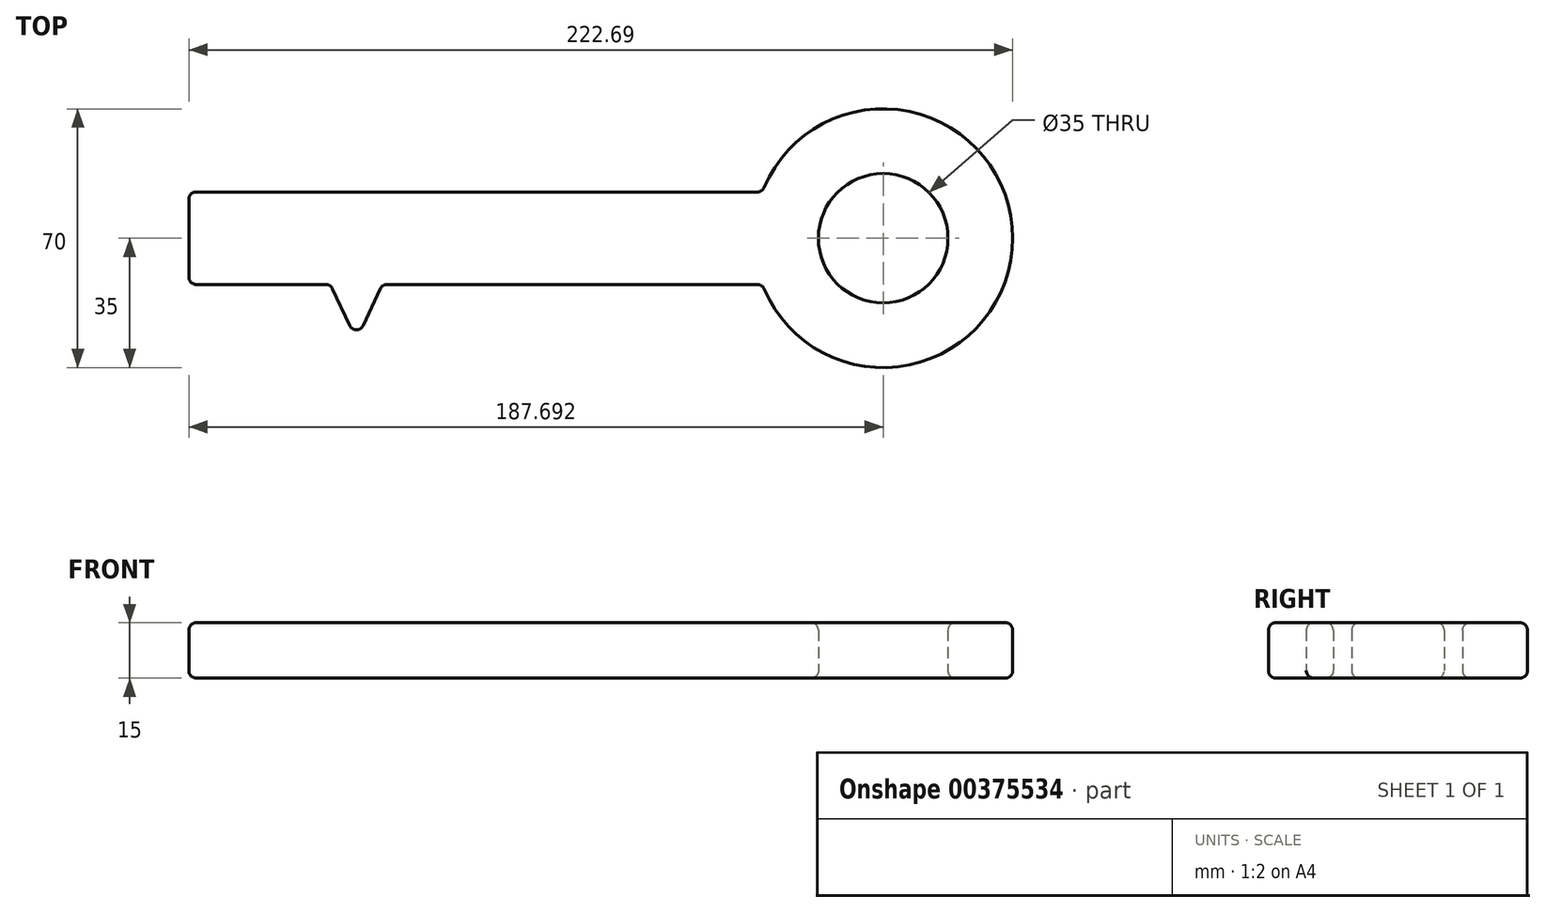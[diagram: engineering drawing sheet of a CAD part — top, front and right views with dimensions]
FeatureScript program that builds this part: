
annotation { "Feature Type Name" : "Feature", "Feature Type Description" : "" }
export const myFeature = defineFeature(function(context is Context, id is Id, definition is map)
    precondition{}
    {
        {
            var Q0;
            Q0=qCreatedBy(makeId("Top.planeOp"),FACE);
            var sketch = newSketch(context, id + "F0", { "sketchPlane" : qUnion([Q0])});
            skLineSegment(sketch, "E0.bottom", {"start": v(-94.78, 40) * mm, "end": v(60.22, 40) * mm});
            skLineSegment(sketch, "E0.top", {"start": v(-94.78, 15) * mm, "end": v(60.22, 15) * mm});
            skLineSegment(sketch, "E0.left", {"start": v(-94.78, 40) * mm, "end": v(-94.78, 15) * mm});
            skLineSegment(sketch, "E1.bottom", {"start": v(-94.49, 15) * mm, "end": v(-84.49, 15) * mm});
            skLineSegment(sketch, "E1.top", {"start": v(-94.49, -15) * mm, "end": v(-84.49, -15) * mm});
            skLineSegment(sketch, "E1.left", {"start": v(-94.49, 15) * mm, "end": v(-94.49, -15) * mm});
            skLineSegment(sketch, "E1.right", {"start": v(-84.49, 15) * mm, "end": v(-84.49, -15) * mm});
            skLineSegment(sketch, "E2.bottom", {"start": v(-74.49, 15) * mm, "end": v(-66.49, 15) * mm});
            skLineSegment(sketch, "E2.top", {"start": v(-74.49, 0) * mm, "end": v(-66.49, 0) * mm});
            skLineSegment(sketch, "E2.left", {"start": v(-74.49, 15) * mm, "end": v(-74.49, 0) * mm});
            skLineSegment(sketch, "E2.right", {"start": v(-66.49, 15) * mm, "end": v(-66.49, 0) * mm});
            skLineSegment(sketch, "E3", {"start": v(-56.49, 15) * mm, "end": v(-49.49, 0) * mm});
            skLineSegment(sketch, "E4", {"start": v(-49.49, 0) * mm, "end": v(-42.49, 15) * mm});
            skArc(sketch, "E5", {"start": v(60.22, 15) * mm, "mid": v(127.91, 27.5) * mm, "end": v(60.22, 40) * mm});
            skCircle(sketch, "E6", {"center": v(92.91, 27.5) * mm, "radius": 17.5 * mm});
            skLineSegment(sketch, "E7", {"start": v(-94.78, 27.5) * mm, "end": v(92.91, 27.5) * mm, "construction": true});
            skSolve(sketch);
        }
        {
            var Q0;
            Q0=makeQuery(id+"F0.imprint","IMPRINT",FACE,{"disambiguationData":[TD([[makeQuery(id+"F0.imprint","IMPRINT",EDGE,{"derivedFrom":sQuery(id+"F0.wireOp",EDGE,"E0.bottom")}),-1.0]])]});
            var Q1;
            Q1=makeQuery(id+"F0.imprint","IMPRINT",FACE,{"disambiguationData":[TD([[makeQuery(id+"F0.imprint","IMPRINT",EDGE,{"derivedFrom":sQuery(id+"F0.wireOp",EDGE,"E1.bottom")}),-1.0]])]});
            var Q2;
            Q2=makeQuery(id+"F0.imprint","IMPRINT",FACE,{"disambiguationData":[TD([[makeQuery(id+"F0.imprint","IMPRINT",EDGE,{"derivedFrom":sQuery(id+"F0.wireOp",EDGE,"E2.bottom")}),-1.0]])]});
            var Q3;
            {var subQ0=sQuery(id+"F0.wireOp",EDGE,"E3");Q3=makeQuery(id+"F0.imprint","IMPRINT",FACE,{"disambiguationData":[TD([[makeQuery(id+"F0.imprint","IMPRINT",EDGE,{"derivedFrom":subQ0}),1.0]])]});}
            extrude(context, id + "F1", {"entities" : qUnion([Q0, Q1, Q2, Q3]), "depth" : 15 * mm});
        }
        {
            var Q0;
            Q0=makeQuery(id+"F1.opExtrude","CAP_EDGE",EDGE,{"disambiguationData":[OSD([sQuery(id+"F0.wireOp",EDGE,"E0.bottom")])],"isStart":false});
            var Q1;
            Q1=makeQuery(id+"F1.opExtrude","CAP_EDGE",EDGE,{"disambiguationData":[OSD([sQuery(id+"F0.wireOp",EDGE,"E1.top")])],"isStart":false});
            var Q2;
            Q2=makeQuery(id+"F1.opExtrude","CAP_EDGE",EDGE,{"disambiguationData":[OSD([sQuery(id+"F0.wireOp",EDGE,"E1.right")])],"isStart":false});
            var Q3;
            {var subQ0=sQuery(id+"F0.wireOp",EDGE,"E0.top");Q3=makeQuery(id+"F1.opExtrude","CAP_EDGE",EDGE,{"disambiguationData":[OSD([subQ0]),TDD([makeQuery(id+"F0.imprint","IMPRINT",EDGE,{"disambiguationData":[TD([[makeQuery(id+"F0.imprint","INTERSECT",VERTEX,{"derivedFrom":[subQ0,sQuery(id+"F0.wireOp",EDGE,"E1.bottom"),sQuery(id+"F0.wireOp",EDGE,"E1.right")]}),-1.0]])],"derivedFrom":subQ0})])],"isStart":false});}
            var Q4;
            {var subQ0=sQuery(id+"F0.wireOp",EDGE,"E0.top");Q4=makeQuery(id+"F1.opExtrude","CAP_EDGE",EDGE,{"disambiguationData":[OSD([subQ0]),TDD([makeQuery(id+"F0.imprint","IMPRINT",EDGE,{"disambiguationData":[TD([[makeQuery(id+"F0.imprint","INTERSECT",VERTEX,{"derivedFrom":[subQ0,sQuery(id+"F0.wireOp",EDGE,"E3")]}),1.0]])],"derivedFrom":subQ0})])],"isStart":false});}
            var Q5;
            Q5=makeQuery(id+"F1.opExtrude","CAP_EDGE",EDGE,{"disambiguationData":[OSD([sQuery(id+"F0.wireOp",EDGE,"E4")])],"isStart":false});
            var Q6;
            Q6=makeQuery(id+"F1.opExtrude","CAP_EDGE",EDGE,{"disambiguationData":[OSD([sQuery(id+"F0.wireOp",EDGE,"E5")])],"isStart":false});
            var Q7;
            Q7=makeQuery(id+"F1.opExtrude","CAP_EDGE",EDGE,{"disambiguationData":[OSD([sQuery(id+"F0.wireOp",EDGE,"E2.top")])],"isStart":false});
            var Q8;
            Q8=makeQuery(id+"F1.opExtrude","CAP_EDGE",EDGE,{"disambiguationData":[OSD([sQuery(id+"F0.wireOp",EDGE,"E1.left")])],"isStart":false});
            var Q9;
            Q9=makeQuery(id+"F1.opExtrude","CAP_EDGE",EDGE,{"disambiguationData":[OSD([sQuery(id+"F0.wireOp",EDGE,"E2.left")])],"isStart":false});
            var Q10;
            Q10=makeQuery(id+"F1.opExtrude","CAP_EDGE",EDGE,{"disambiguationData":[OSD([sQuery(id+"F0.wireOp",EDGE,"E2.right")])],"isStart":false});
            var Q11;
            Q11=makeQuery(id+"F1.opExtrude","CAP_EDGE",EDGE,{"disambiguationData":[OSD([sQuery(id+"F0.wireOp",EDGE,"E5")])],"isStart":true});
            var Q12;
            Q12=makeQuery(id+"F1.opExtrude","CAP_EDGE",EDGE,{"disambiguationData":[OSD([sQuery(id+"F0.wireOp",EDGE,"E6")])],"isStart":true});
            var Q13;
            Q13=makeQuery(id+"F1.opExtrude","SWEPT_FACE",FACE,{"disambiguationData":[OSD([sQuery(id+"F0.wireOp",EDGE,"E6")])]});
            var Q14;
            {var subQ0=sQuery(id+"F0.wireOp",EDGE,"E0.top");Q14=makeQuery(id+"F1.opExtrude","CAP_EDGE",EDGE,{"disambiguationData":[OSD([subQ0]),TDD([makeQuery(id+"F0.imprint","IMPRINT",EDGE,{"disambiguationData":[TD([[makeQuery(id+"F0.imprint","INTERSECT",VERTEX,{"derivedFrom":[subQ0,sQuery(id+"F0.wireOp",EDGE,"E5")]}),1.0]])],"derivedFrom":subQ0})])],"isStart":true});}
            var Q15;
            {var subQ0=sQuery(id+"F0.wireOp",EDGE,"E0.top");Q15=makeQuery(id+"F1.opExtrude","CAP_EDGE",EDGE,{"disambiguationData":[OSD([subQ0]),TDD([makeQuery(id+"F0.imprint","IMPRINT",EDGE,{"disambiguationData":[TD([[makeQuery(id+"F0.imprint","INTERSECT",VERTEX,{"derivedFrom":[subQ0,sQuery(id+"F0.wireOp",EDGE,"E5")]}),1.0]])],"derivedFrom":subQ0})])],"isStart":false});}
            var Q16;
            Q16=makeQuery(id+"F1.opExtrude","SWEPT_EDGE",EDGE,{"disambiguationData":[OSD([sQuery(id+"F0.wireOp",EDGE,"E0.bottom"),sQuery(id+"F0.wireOp",EDGE,"E5")])]});
            var Q17;
            Q17=makeQuery(id+"F1.opExtrude","CAP_EDGE",EDGE,{"disambiguationData":[OSD([sQuery(id+"F0.wireOp",EDGE,"E4")])],"isStart":true});
            var Q18;
            Q18=makeQuery(id+"F1.opExtrude","SWEPT_EDGE",EDGE,{"disambiguationData":[OSD([sQuery(id+"F0.wireOp",EDGE,"E0.top"),sQuery(id+"F0.wireOp",EDGE,"E4")])]});
            var Q19;
            Q19=makeQuery(id+"F1.opExtrude","SWEPT_EDGE",EDGE,{"disambiguationData":[OSD([sQuery(id+"F0.wireOp",EDGE,"E0.top"),sQuery(id+"F0.wireOp",EDGE,"E3")])]});
            var Q20;
            Q20=makeQuery(id+"F1.opExtrude","CAP_EDGE",EDGE,{"disambiguationData":[OSD([sQuery(id+"F0.wireOp",EDGE,"E3")])],"isStart":true});
            var Q21;
            Q21=makeQuery(id+"F1.opExtrude","CAP_EDGE",EDGE,{"disambiguationData":[OSD([sQuery(id+"F0.wireOp",EDGE,"E0.bottom")])],"isStart":true});
            var Q22;
            Q22=makeQuery(id+"F1.opExtrude","CAP_EDGE",EDGE,{"disambiguationData":[OSD([sQuery(id+"F0.wireOp",EDGE,"E6")])],"isStart":false});
            var Q23;
            Q23=makeQuery(id+"F1.opExtrude","SWEPT_EDGE",EDGE,{"disambiguationData":[OSD([sQuery(id+"F0.wireOp",EDGE,"E0.bottom"),sQuery(id+"F0.wireOp",EDGE,"E0.left")])]});
            var Q24;
            Q24=makeQuery(id+"F1.opExtrude","CAP_EDGE",EDGE,{"disambiguationData":[OSD([sQuery(id+"F0.wireOp",EDGE,"E0.left")])],"isStart":true});
            var Q25;
            Q25=makeQuery(id+"F1.opExtrude","CAP_EDGE",EDGE,{"disambiguationData":[OSD([sQuery(id+"F0.wireOp",EDGE,"E2.right")])],"isStart":true});
            var Q26;
            {var subQ0=sQuery(id+"F0.wireOp",EDGE,"E0.top");Q26=makeQuery(id+"F1.opExtrude","CAP_EDGE",EDGE,{"disambiguationData":[OSD([subQ0]),TDD([makeQuery(id+"F0.imprint","IMPRINT",EDGE,{"disambiguationData":[TD([[makeQuery(id+"F0.imprint","INTERSECT",VERTEX,{"derivedFrom":[subQ0,sQuery(id+"F0.wireOp",EDGE,"E1.bottom"),sQuery(id+"F0.wireOp",EDGE,"E1.right")]}),-1.0]])],"derivedFrom":subQ0})])],"isStart":true});}
            var Q27;
            Q27=makeQuery(id+"F1.opExtrude","CAP_EDGE",EDGE,{"disambiguationData":[OSD([sQuery(id+"F0.wireOp",EDGE,"E1.right")])],"isStart":true});
            var Q28;
            Q28=makeQuery(id+"F1.opExtrude","SWEPT_EDGE",EDGE,{"disambiguationData":[OSD([sQuery(id+"F0.wireOp",EDGE,"E3"),sQuery(id+"F0.wireOp",EDGE,"E4")])]});
            var Q29;
            Q29=makeQuery(id+"F1.opExtrude","SWEPT_EDGE",EDGE,{"disambiguationData":[OSD([sQuery(id+"F0.wireOp",EDGE,"E2.top"),sQuery(id+"F0.wireOp",EDGE,"E2.left")])]});
            var Q30;
            Q30=makeQuery(id+"F1.opExtrude","CAP_EDGE",EDGE,{"disambiguationData":[OSD([sQuery(id+"F0.wireOp",EDGE,"E1.left")])],"isStart":true});
            var Q31;
            Q31=makeQuery(id+"F1.opExtrude","SWEPT_EDGE",EDGE,{"disambiguationData":[OSD([sQuery(id+"F0.wireOp",EDGE,"E1.top"),sQuery(id+"F0.wireOp",EDGE,"E1.right")])]});
            var Q32;
            Q32=makeQuery(id+"F1.opExtrude","SWEPT_EDGE",EDGE,{"disambiguationData":[OSD([sQuery(id+"F0.wireOp",EDGE,"E1.top"),sQuery(id+"F0.wireOp",EDGE,"E1.left")])]});
            var Q33;
            Q33=makeQuery(id+"F1.opExtrude","CAP_EDGE",EDGE,{"disambiguationData":[OSD([sQuery(id+"F0.wireOp",EDGE,"E3")])],"isStart":false});
            var Q34;
            Q34=makeQuery(id+"F1.opExtrude","SWEPT_EDGE",EDGE,{"disambiguationData":[OSD([sQuery(id+"F0.wireOp",EDGE,"E0.top"),sQuery(id+"F0.wireOp",EDGE,"E0.left")])]});
            var Q35;
            Q35=makeQuery(id+"F1.opExtrude","SWEPT_EDGE",EDGE,{"disambiguationData":[OSD([sQuery(id+"F0.wireOp",EDGE,"E0.top"),sQuery(id+"F0.wireOp",EDGE,"E2.bottom"),sQuery(id+"F0.wireOp",EDGE,"E2.right")])]});
            var Q36;
            Q36=makeQuery(id+"F1.opExtrude","SWEPT_EDGE",EDGE,{"disambiguationData":[OSD([sQuery(id+"F0.wireOp",EDGE,"E2.top"),sQuery(id+"F0.wireOp",EDGE,"E2.right")])]});
            var Q37;
            Q37=makeQuery(id+"F1.opExtrude","SWEPT_EDGE",EDGE,{"disambiguationData":[OSD([sQuery(id+"F0.wireOp",EDGE,"E0.top"),sQuery(id+"F0.wireOp",EDGE,"E1.bottom"),sQuery(id+"F0.wireOp",EDGE,"E1.right")])]});
            var Q38;
            Q38=makeQuery(id+"F1.opExtrude","SWEPT_EDGE",EDGE,{"disambiguationData":[OSD([sQuery(id+"F0.wireOp",EDGE,"E0.top"),sQuery(id+"F0.wireOp",EDGE,"E5")])]});
            var Q39;
            Q39=makeQuery(id+"F1.opExtrude","CAP_EDGE",EDGE,{"disambiguationData":[OSD([sQuery(id+"F0.wireOp",EDGE,"E2.left")])],"isStart":true});
            var Q40;
            {var subQ0=sQuery(id+"F0.wireOp",EDGE,"E0.top");Q40=makeQuery(id+"F1.opExtrude","CAP_EDGE",EDGE,{"disambiguationData":[OSD([subQ0]),TDD([makeQuery(id+"F0.imprint","IMPRINT",EDGE,{"disambiguationData":[TD([[makeQuery(id+"F0.imprint","INTERSECT",VERTEX,{"derivedFrom":[subQ0,sQuery(id+"F0.wireOp",EDGE,"E3")]}),1.0]])],"derivedFrom":subQ0})])],"isStart":true});}
            var Q41;
            Q41=makeQuery(id+"F1.opExtrude","CAP_EDGE",EDGE,{"disambiguationData":[OSD([sQuery(id+"F0.wireOp",EDGE,"E2.top")])],"isStart":true});
            var Q42;
            Q42=makeQuery(id+"F1.opExtrude","CAP_EDGE",EDGE,{"disambiguationData":[OSD([sQuery(id+"F0.wireOp",EDGE,"E1.top")])],"isStart":true});
            var Q43;
            Q43=makeQuery(id+"F1.opExtrude","CAP_EDGE",EDGE,{"disambiguationData":[OSD([sQuery(id+"F0.wireOp",EDGE,"E0.left")])],"isStart":false});
            var Q44;
            Q44=makeQuery(id+"F1.opExtrude","SWEPT_EDGE",EDGE,{"disambiguationData":[OSD([sQuery(id+"F0.wireOp",EDGE,"E0.top"),sQuery(id+"F0.wireOp",EDGE,"E2.bottom"),sQuery(id+"F0.wireOp",EDGE,"E2.left")])]});
            fillet(context, id + "F2", {"entities" : qUnion([Q0, Q1, Q2, Q3, Q4, Q5, Q6, Q7, Q8, Q9, Q10, Q11, Q12, Q13, Q14, Q15, Q16, Q17, Q18, Q19, Q20, Q21, Q22, Q23, Q24, Q25, Q26, Q27, Q28, Q29, Q30, Q31, Q32, Q33, Q34, Q35, Q36, Q37, Q38, Q39, Q40, Q41, Q42, Q43, Q44]), "radius" : 2 * mm, "tangentPropagation" : true, "allowEdgeOverflow" : false});
        }
    });
